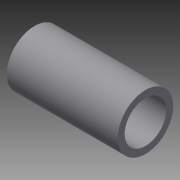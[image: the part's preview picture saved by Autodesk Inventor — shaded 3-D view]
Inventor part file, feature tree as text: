
AUTODESK INVENTOR PART (.ipt)
format: ipt  version: 2015 SP1 (Build 190203100, 203)  size: 80,384 bytes
history: native  units: in
note: dims shown in document units (in); Inventor stores cm internally (conversion verified against a paired STEP export)
features: extrude x1, sketch x1
ambient origin geometry x8: Origin, YZ Plane, XZ Plane, XY Plane, X Axis, Y Axis, Z Axis, Center Point
bodies: Solid1 (feature_tree)
feature tree (2):
  extrude  "Extrusion1"  Depth=1.0in
  sketch  "Sketch1"  dims[d0=0.375in d1=0.5in d2=1.0in d3=0.0in]
